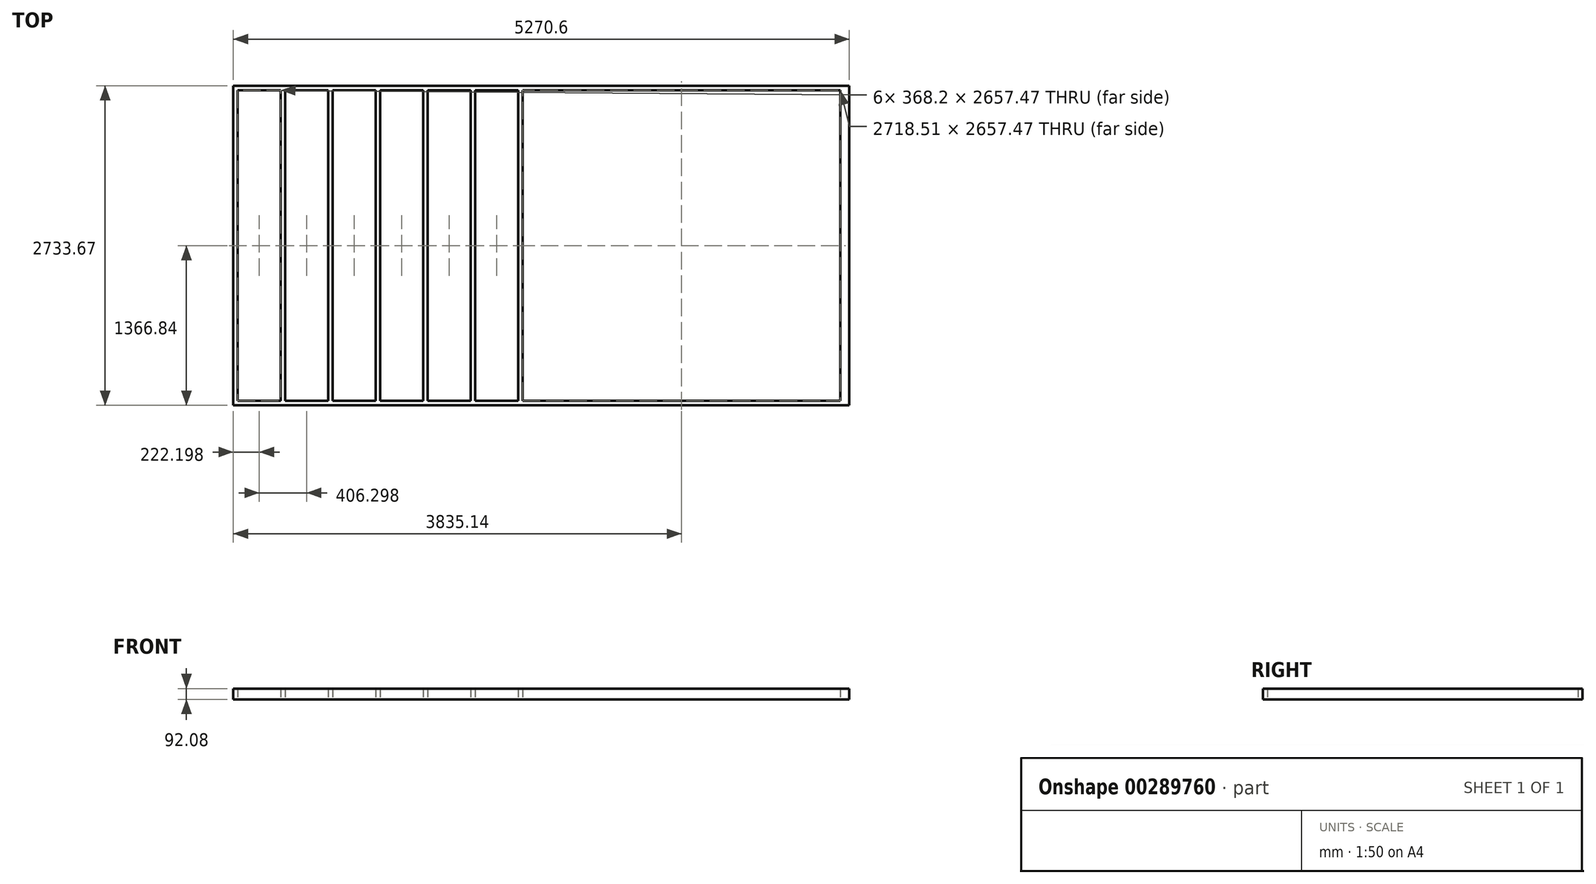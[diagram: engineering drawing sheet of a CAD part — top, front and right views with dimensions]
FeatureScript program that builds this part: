
annotation { "Feature Type Name" : "Feature", "Feature Type Description" : "" }
export const myFeature = defineFeature(function(context is Context, id is Id, definition is map)
    precondition{}
    {
        {
            var Q0;
            Q0=qCreatedBy(makeId("Top.planeOp"),FACE);
            var sketch = newSketch(context, id + "F0", { "sketchPlane" : qUnion([Q0])});
            skLineSegment(sketch, "E0.right", {"start": v(-5575.4, -1219.2) * mm, "end": v(-5575.4, 1514.47) * mm});
            skPoint(sketch, "E0.middle", {"position": v(0, 0) * mm});
            skLineSegment(sketch, "E1", {"start": v(-304.8, 1514.48) * mm, "end": v(-304.8, -1219.2) * mm});
            skLineSegment(sketch, "E2", {"start": v(-5575.4, -1219.2) * mm, "end": v(-304.8, -1219.2) * mm});
            skLineSegment(sketch, "E3.bottom", {"start": v(-5537.3, 1476.37) * mm, "end": v(-342.9, 1476.37) * mm});
            skLineSegment(sketch, "E3.top", {"start": v(-5537.3, -1181.1) * mm, "end": v(-342.9, -1181.1) * mm});
            skLineSegment(sketch, "E3.left", {"start": v(-5537.3, 1476.37) * mm, "end": v(-5537.3, -1181.1) * mm});
            skLineSegment(sketch, "E3.right", {"start": v(-342.9, 1476.38) * mm, "end": v(-342.9, -1181.1) * mm});
            skLineSegment(sketch, "E4.bottom", {"start": v(-5169.1, 1476.37) * mm, "end": v(-5131, 1476.37) * mm});
            skLineSegment(sketch, "E4.top", {"start": v(-5169.1, -1181.1) * mm, "end": v(-5131, -1181.1) * mm});
            skLineSegment(sketch, "E4.left", {"start": v(-5169.1, 1476.37) * mm, "end": v(-5169.1, -1181.1) * mm});
            skLineSegment(sketch, "E4.right", {"start": v(-5131, 1476.37) * mm, "end": v(-5131, -1181.1) * mm});
            skLineSegment(sketch, "E5.bottom", {"start": v(-4762.8, 1476.37) * mm, "end": v(-4724.7, 1476.37) * mm});
            skLineSegment(sketch, "E5.top", {"start": v(-4762.8, -1181.1) * mm, "end": v(-4724.7, -1181.1) * mm});
            skLineSegment(sketch, "E5.left", {"start": v(-4762.8, 1476.37) * mm, "end": v(-4762.8, -1181.1) * mm});
            skLineSegment(sketch, "E5.right", {"start": v(-4724.7, 1476.37) * mm, "end": v(-4724.7, -1181.1) * mm});
            skLineSegment(sketch, "E6.bottom", {"start": v(-4356.5, 1476.37) * mm, "end": v(-4318.4, 1476.37) * mm});
            skLineSegment(sketch, "E6.top", {"start": v(-4356.5, -1181.1) * mm, "end": v(-4318.4, -1181.1) * mm});
            skLineSegment(sketch, "E6.left", {"start": v(-4356.5, 1476.37) * mm, "end": v(-4356.5, -1181.1) * mm});
            skLineSegment(sketch, "E6.right", {"start": v(-4318.4, 1476.37) * mm, "end": v(-4318.4, -1181.1) * mm});
            skLineSegment(sketch, "E7.bottom", {"start": v(-3950.2, 1476.37) * mm, "end": v(-3912.1, 1476.37) * mm});
            skLineSegment(sketch, "E7.top", {"start": v(-3950.2, -1181.1) * mm, "end": v(-3912.1, -1181.1) * mm});
            skLineSegment(sketch, "E7.left", {"start": v(-3950.2, 1476.37) * mm, "end": v(-3950.2, -1181.1) * mm});
            skLineSegment(sketch, "E7.right", {"start": v(-3912.1, 1476.37) * mm, "end": v(-3912.1, -1181.1) * mm});
            skLineSegment(sketch, "E8.bottom", {"start": v(-3543.9, 1476.38) * mm, "end": v(-3505.8, 1476.38) * mm});
            skLineSegment(sketch, "E8.top", {"start": v(-3543.9, -1181.1) * mm, "end": v(-3505.8, -1181.1) * mm});
            skLineSegment(sketch, "E8.left", {"start": v(-3543.9, 1476.37) * mm, "end": v(-3543.9, -1181.1) * mm});
            skLineSegment(sketch, "E8.right", {"start": v(-3505.8, 1476.37) * mm, "end": v(-3505.8, -1181.1) * mm});
            skLineSegment(sketch, "E9.bottom", {"start": v(-3137.61, 1476.38) * mm, "end": v(-3099.51, 1476.38) * mm});
            skLineSegment(sketch, "E9.top", {"start": v(-3137.61, -1181.1) * mm, "end": v(-3099.51, -1181.1) * mm});
            skLineSegment(sketch, "E9.left", {"start": v(-3137.61, 1476.37) * mm, "end": v(-3137.61, -1181.1) * mm});
            skLineSegment(sketch, "E9.right", {"start": v(-3099.51, 1476.37) * mm, "end": v(-3099.51, -1181.1) * mm});
            skLineSegment(sketch, "E10", {"start": v(-3118.56, 1476.37) * mm, "end": v(-3118.56, -1181.1) * mm, "construction": true});
            skLineSegment(sketch, "E11.MirrorCS", {"start": v(-1068.02, 1476.38) * mm, "end": v(-1106.12, 1476.38) * mm});
            skLineSegment(sketch, "E12.MirrorCS", {"start": v(-1068.02, -1181.1) * mm, "end": v(-1106.12, -1181.1) * mm});
            skLineSegment(sketch, "E13.MirrorCS", {"start": v(-2693.21, -1181.1) * mm, "end": v(-2731.31, -1181.1) * mm});
            skLineSegment(sketch, "E14.MirrorCS", {"start": v(-1880.62, -1181.1) * mm, "end": v(-1918.72, -1181.1) * mm});
            skLineSegment(sketch, "E15.MirrorCS", {"start": v(-1880.62, 1476.38) * mm, "end": v(-1918.72, 1476.38) * mm});
            skLineSegment(sketch, "E16.MirrorCS", {"start": v(-1474.32, 1476.38) * mm, "end": v(-1512.42, 1476.38) * mm});
            skLineSegment(sketch, "E17.MirrorCS", {"start": v(-2286.91, 1476.38) * mm, "end": v(-2325.01, 1476.38) * mm});
            skLineSegment(sketch, "E18.MirrorCS", {"start": v(-2693.21, 1476.38) * mm, "end": v(-2731.31, 1476.38) * mm});
            skLineSegment(sketch, "E19.MirrorCS", {"start": v(-1474.32, -1181.1) * mm, "end": v(-1512.42, -1181.1) * mm});
            skLineSegment(sketch, "E20.MirrorCS", {"start": v(-2286.91, -1181.1) * mm, "end": v(-2325.01, -1181.1) * mm});
            skLineSegment(sketch, "E21.MirrorCS", {"start": v(-1474.32, 1476.38) * mm, "end": v(-1474.32, -1181.1) * mm});
            skLineSegment(sketch, "E22.MirrorCS", {"start": v(-2325.01, 1476.37) * mm, "end": v(-2325.01, -1181.1) * mm});
            skLineSegment(sketch, "E23.MirrorCS", {"start": v(-1068.02, 1476.38) * mm, "end": v(-1068.02, -1181.1) * mm});
            skLineSegment(sketch, "E24.MirrorCS", {"start": v(-1512.42, 1476.38) * mm, "end": v(-1512.42, -1181.1) * mm});
            skLineSegment(sketch, "E25.MirrorCS", {"start": v(-1918.72, 1476.37) * mm, "end": v(-1918.72, -1181.1) * mm});
            skLineSegment(sketch, "E26.MirrorCS", {"start": v(-2693.21, 1476.37) * mm, "end": v(-2693.21, -1181.1) * mm});
            skLineSegment(sketch, "E27.MirrorCS", {"start": v(-2286.91, 1476.37) * mm, "end": v(-2286.91, -1181.1) * mm});
            skLineSegment(sketch, "E28.MirrorCS", {"start": v(-1106.12, 1476.37) * mm, "end": v(-1106.12, -1181.1) * mm});
            skLineSegment(sketch, "E29.MirrorCS", {"start": v(-2731.31, 1476.37) * mm, "end": v(-2731.31, -1181.1) * mm});
            skLineSegment(sketch, "E30.MirrorCS", {"start": v(-1880.62, 1476.37) * mm, "end": v(-1880.62, -1181.1) * mm});
            skLineSegment(sketch, "E31", {"start": v(-5575.4, 1514.47) * mm, "end": v(-304.8, 1514.48) * mm});
            skLineSegment(sketch, "E32", {"start": v(-381, 1476.38) * mm, "end": v(-381, -1181.1) * mm});
            skLineSegment(sketch, "E33.bottom", {"start": v(-699.82, 1476.37) * mm, "end": v(-661.72, 1476.37) * mm});
            skLineSegment(sketch, "E33.top", {"start": v(-699.82, -1181.1) * mm, "end": v(-661.72, -1181.1) * mm});
            skLineSegment(sketch, "E33.left", {"start": v(-699.82, 1476.38) * mm, "end": v(-699.82, -1181.1) * mm});
            skLineSegment(sketch, "E33.right", {"start": v(-661.72, 1476.38) * mm, "end": v(-661.72, -1181.1) * mm});
            skSolve(sketch);
        }
        {
            var Q0;
            {var subQ0=sQuery(id+"F0.wireOp",EDGE,"kg6uHfn1-oYHp-dpYk-6MLj-0RLF3WtnhEy7");var subQ1=sQuery(id+"F0.wireOp",EDGE,"8106601b-d97d-4dcf-b6dc-423d0e0e66910.MirrorCS");var subQ2=makeQuery(id+"F0.imprint","INTERSECT",VERTEX,{"derivedFrom":[subQ1,subQ0]});Q0=makeQuery(id+"F0.imprint","IMPRINT",FACE,{"disambiguationData":[TD([[makeQuery(id+"F0.imprint","IMPRINT",EDGE,{"disambiguationData":[TD([[subQ2,-1.0]])],"derivedFrom":subQ1}),1.0]])]});}
            var Q1;
            Q1=makeQuery(id+"F0.imprint","IMPRINT",FACE,{"disambiguationData":[TD([[makeQuery(id+"F0.imprint","IMPRINT",EDGE,{"derivedFrom":sQuery(id+"F0.wireOp",EDGE,"w7in2STq-dmfq-Ztst-uc13-PS53EKAe34f7.bottom")}),-1.0]])]});
            var Q2;
            {var subQ4=sQuery(id+"F0.wireOp",EDGE,"8a681850-bd4a-4ca6-8d45-30870cc5114b0.MirrorCS");var subQ6=sQuery(id+"F0.wireOp",EDGE,"4AthFqkJ-wqFj-7w0H-RTdV-ZVLi3eRejgEJ.bottom");var subQ7=makeQuery(id+"F0.imprint","INTERSECT",VERTEX,{"derivedFrom":[subQ6,subQ4]});Q2=makeQuery(id+"F0.imprint","IMPRINT",FACE,{"disambiguationData":[TD([[makeQuery(id+"F0.imprint","IMPRINT",EDGE,{"disambiguationData":[TD([[subQ7,-1.0]])],"derivedFrom":subQ6}),1.0]])]});}
            var Q3;
            {var subQ5=sQuery(id+"F0.wireOp",EDGE,"eca8af08-4f88-4f9e-b7fb-055b73c8b4f30.MirrorCS");var subQ7=sQuery(id+"F0.wireOp",EDGE,"4AthFqkJ-wqFj-7w0H-RTdV-ZVLi3eRejgEJ.bottom");var subQ8=makeQuery(id+"F0.imprint","INTERSECT",VERTEX,{"derivedFrom":[subQ7,subQ5]});Q3=makeQuery(id+"F0.imprint","IMPRINT",FACE,{"disambiguationData":[TD([[makeQuery(id+"F0.imprint","IMPRINT",EDGE,{"disambiguationData":[TD([[subQ8,-1.0]])],"derivedFrom":subQ7}),1.0]])]});}
            var Q4;
            {var subQ4=sQuery(id+"F0.wireOp",EDGE,"1bcce820-757c-45ce-a4fe-54bff22ba8310.MirrorCS");var subQ6=sQuery(id+"F0.wireOp",EDGE,"4AthFqkJ-wqFj-7w0H-RTdV-ZVLi3eRejgEJ.bottom");var subQ7=makeQuery(id+"F0.imprint","INTERSECT",VERTEX,{"derivedFrom":[subQ6,subQ4]});Q4=makeQuery(id+"F0.imprint","IMPRINT",FACE,{"disambiguationData":[TD([[makeQuery(id+"F0.imprint","IMPRINT",EDGE,{"disambiguationData":[TD([[subQ7,-1.0]])],"derivedFrom":subQ6}),1.0]])]});}
            var Q5;
            {var subQ4=sQuery(id+"F0.wireOp",EDGE,"4AthFqkJ-wqFj-7w0H-RTdV-ZVLi3eRejgEJ.left");Q5=makeQuery(id+"F0.imprint","IMPRINT",FACE,{"disambiguationData":[TD([[makeQuery(id+"F0.imprint","IMPRINT",EDGE,{"derivedFrom":subQ4}),-1.0]])]});}
            var Q6;
            {var subQ4=sQuery(id+"F0.wireOp",EDGE,"1XwIb5Eg-bF9u-TIWm-DKcX-weKEORKnCqGm.bottom");var subQ7=sQuery(id+"F0.wireOp",EDGE,"1bcce820-757c-45ce-a4fe-54bff22ba8310.MirrorCS");var subQ10=makeQuery(id+"F0.imprint","INTERSECT",VERTEX,{"derivedFrom":[subQ4,subQ7]});Q6=makeQuery(id+"F0.imprint","IMPRINT",FACE,{"disambiguationData":[TD([[makeQuery(id+"F0.imprint","IMPRINT",EDGE,{"disambiguationData":[TD([[subQ10,-1.0]])],"derivedFrom":subQ4}),-1.0]])]});}
            var Q7;
            {var subQ6=sQuery(id+"F0.wireOp",EDGE,"1XwIb5Eg-bF9u-TIWm-DKcX-weKEORKnCqGm.left");Q7=makeQuery(id+"F0.imprint","IMPRINT",FACE,{"disambiguationData":[TD([[makeQuery(id+"F0.imprint","IMPRINT",EDGE,{"derivedFrom":subQ6}),1.0]])]});}
            var Q8;
            {var subQ4=sQuery(id+"F0.wireOp",EDGE,"1XwIb5Eg-bF9u-TIWm-DKcX-weKEORKnCqGm.bottom");var subQ7=sQuery(id+"F0.wireOp",EDGE,"eca8af08-4f88-4f9e-b7fb-055b73c8b4f30.MirrorCS");var subQ9=makeQuery(id+"F0.imprint","INTERSECT",VERTEX,{"derivedFrom":[subQ4,subQ7]});Q8=makeQuery(id+"F0.imprint","IMPRINT",FACE,{"disambiguationData":[TD([[makeQuery(id+"F0.imprint","IMPRINT",EDGE,{"disambiguationData":[TD([[subQ9,-1.0]])],"derivedFrom":subQ4}),-1.0]])]});}
            var Q9;
            {var subQ3=sQuery(id+"F0.wireOp",EDGE,"8a681850-bd4a-4ca6-8d45-30870cc5114b0.MirrorCS");var subQ6=sQuery(id+"F0.wireOp",EDGE,"1XwIb5Eg-bF9u-TIWm-DKcX-weKEORKnCqGm.bottom");var subQ7=makeQuery(id+"F0.imprint","INTERSECT",VERTEX,{"derivedFrom":[subQ6,subQ3]});Q9=makeQuery(id+"F0.imprint","IMPRINT",FACE,{"disambiguationData":[TD([[makeQuery(id+"F0.imprint","IMPRINT",EDGE,{"disambiguationData":[TD([[subQ7,-1.0]])],"derivedFrom":subQ6}),-1.0]])]});}
            var Q10;
            {var subQ0=sQuery(id+"F0.wireOp",EDGE,"573c87d8-b675-496e-a079-9395e3357b8d0.MirrorCS");Q10=makeQuery(id+"F0.imprint","IMPRINT",FACE,{"disambiguationData":[TD([[makeQuery(id+"F0.imprint","IMPRINT",EDGE,{"derivedFrom":subQ0}),1.0]])]});}
            var Q11;
            {var subQ0=sQuery(id+"F0.wireOp",EDGE,"edbdd21b-7951-4497-ac7e-6e46abb4ccd70.MirrorCS");Q11=makeQuery(id+"F0.imprint","IMPRINT",FACE,{"disambiguationData":[TD([[makeQuery(id+"F0.imprint","IMPRINT",EDGE,{"derivedFrom":subQ0}),-1.0]])]});}
            var Q12;
            Q12=makeQuery(id+"F0.imprint","IMPRINT",FACE,{"disambiguationData":[TD([[makeQuery(id+"F0.imprint","IMPRINT",EDGE,{"derivedFrom":sQuery(id+"F0.wireOp",EDGE,"xTM1oSQN-q9p7-LrQJ-wgkP-syFjsQtJfwuK.bottom")}),-1.0]])]});
            var Q13;
            {var subQ0=sQuery(id+"F0.wireOp",EDGE,"7de17b8e-8469-475a-b975-fd82b060c23f0.MirrorCS");Q13=makeQuery(id+"F0.imprint","IMPRINT",FACE,{"disambiguationData":[TD([[makeQuery(id+"F0.imprint","IMPRINT",EDGE,{"derivedFrom":subQ0}),1.0]])]});}
            var Q14;
            {var subQ0=sQuery(id+"F0.wireOp",EDGE,"e03bbd14-4e46-43d8-a5f9-80b2dea7db7f0.MirrorCS");Q14=makeQuery(id+"F0.imprint","IMPRINT",FACE,{"disambiguationData":[TD([[makeQuery(id+"F0.imprint","IMPRINT",EDGE,{"derivedFrom":subQ0}),1.0]])]});}
            var Q15;
            {var subQ0=sQuery(id+"F0.wireOp",EDGE,"1b0e9755-274d-47f2-9ad2-c5868fe4f0aa0.MirrorCS");Q15=makeQuery(id+"F0.imprint","IMPRINT",FACE,{"disambiguationData":[TD([[makeQuery(id+"F0.imprint","IMPRINT",EDGE,{"derivedFrom":subQ0}),1.0]])]});}
            var Q16;
            {var subQ0=sQuery(id+"F0.wireOp",EDGE,"0493b29f-ec4a-4c4c-ac9e-8fdb3be76d310.MirrorCS");Q16=makeQuery(id+"F0.imprint","IMPRINT",FACE,{"disambiguationData":[TD([[makeQuery(id+"F0.imprint","IMPRINT",EDGE,{"derivedFrom":subQ0}),1.0]])]});}
            var Q17;
            {var subQ0=sQuery(id+"F0.wireOp",EDGE,"9fe0fe99-07bc-4679-9664-f55d6f2dc43d0.MirrorCS");Q17=makeQuery(id+"F0.imprint","IMPRINT",FACE,{"disambiguationData":[TD([[makeQuery(id+"F0.imprint","IMPRINT",EDGE,{"derivedFrom":subQ0}),1.0]])]});}
            var Q18;
            {var subQ7=sQuery(id+"F0.wireOp",EDGE,"1XwIb5Eg-bF9u-TIWm-DKcX-weKEORKnCqGm.right");Q18=makeQuery(id+"F0.imprint","IMPRINT",FACE,{"disambiguationData":[TD([[makeQuery(id+"F0.imprint","IMPRINT",EDGE,{"derivedFrom":subQ7}),-1.0]])]});}
            var Q19;
            {var subQ3=sQuery(id+"F0.wireOp",EDGE,"cGS8tV0A-mpKU-2uX5-CStv-OkKF9vKUYxA9");Q19=makeQuery(id+"F0.imprint","IMPRINT",FACE,{"disambiguationData":[TD([[makeQuery(id+"F0.imprint","IMPRINT",EDGE,{"derivedFrom":subQ3}),1.0]])]});}
            var Q20;
            {var subQ0=sQuery(id+"F0.wireOp",EDGE,"3EoNbSYs-SzWb-u8DF-ybgV-jMauNVkNRy9z.bottom");Q20=makeQuery(id+"F0.imprint","IMPRINT",FACE,{"disambiguationData":[TD([[makeQuery(id+"F0.imprint","IMPRINT",EDGE,{"derivedFrom":subQ0}),1.0]])]});}
            var Q21;
            {var subQ3=sQuery(id+"F0.wireOp",EDGE,"4AthFqkJ-wqFj-7w0H-RTdV-ZVLi3eRejgEJ.right");Q21=makeQuery(id+"F0.imprint","IMPRINT",FACE,{"disambiguationData":[TD([[makeQuery(id+"F0.imprint","IMPRINT",EDGE,{"derivedFrom":subQ3}),1.0]])]});}
            var Q22;
            {var subQ5=sQuery(id+"F0.wireOp",EDGE,"0632b321-56e7-4b31-9cd1-585e07a893ff0.MirrorCS");var subQ6=sQuery(id+"F0.wireOp",EDGE,"1XwIb5Eg-bF9u-TIWm-DKcX-weKEORKnCqGm.bottom");var subQ7=makeQuery(id+"F0.imprint","INTERSECT",VERTEX,{"derivedFrom":[subQ6,subQ5]});Q22=makeQuery(id+"F0.imprint","IMPRINT",FACE,{"disambiguationData":[TD([[makeQuery(id+"F0.imprint","IMPRINT",EDGE,{"disambiguationData":[TD([[subQ7,-1.0]])],"derivedFrom":subQ6}),-1.0]])]});}
            var Q23;
            {var subQ4=sQuery(id+"F0.wireOp",EDGE,"e9220ee2-881e-495c-a7c1-f9c4819509570.MirrorCS");Q23=makeQuery(id+"F0.imprint","IMPRINT",FACE,{"disambiguationData":[TD([[makeQuery(id+"F0.imprint","IMPRINT",EDGE,{"derivedFrom":subQ4}),-1.0]])]});}
            var Q24;
            {var subQ4=sQuery(id+"F0.wireOp",EDGE,"e9220ee2-881e-495c-a7c1-f9c4819509570.MirrorCS");Q24=makeQuery(id+"F0.imprint","IMPRINT",FACE,{"disambiguationData":[TD([[makeQuery(id+"F0.imprint","IMPRINT",EDGE,{"derivedFrom":subQ4}),-1.0]])]});}
            var Q25;
            {var subQ0=sQuery(id+"F0.wireOp",EDGE,"3EoNbSYs-SzWb-u8DF-ybgV-jMauNVkNRy9z.top");Q25=makeQuery(id+"F0.imprint","IMPRINT",FACE,{"disambiguationData":[TD([[makeQuery(id+"F0.imprint","IMPRINT",EDGE,{"derivedFrom":subQ0}),-1.0]])]});}
            var Q26;
            {var subQ0=sQuery(id+"F0.wireOp",EDGE,"aInlmaS3-BiLq-Bbma-6VfX-RYyb0QgMCohg");Q26=makeQuery(id+"F0.imprint","IMPRINT",FACE,{"disambiguationData":[TD([[makeQuery(id+"F0.imprint","IMPRINT",EDGE,{"derivedFrom":subQ0}),1.0]])]});}
            var Q27;
            {var subQ1=sQuery(id+"F0.wireOp",EDGE,"6dIbjfUG-IAKx-LzC9-qQtg-bTm0nvSxZE7U");Q27=makeQuery(id+"F0.imprint","IMPRINT",FACE,{"disambiguationData":[TD([[makeQuery(id+"F0.imprint","IMPRINT",EDGE,{"derivedFrom":subQ1}),-1.0]])]});}
            var Q28;
            {var subQ3=sQuery(id+"F0.wireOp",EDGE,"6dIbjfUG-IAKx-LzC9-qQtg-bTm0nvSxZE7U");Q28=makeQuery(id+"F0.imprint","IMPRINT",FACE,{"disambiguationData":[TD([[makeQuery(id+"F0.imprint","IMPRINT",EDGE,{"derivedFrom":subQ3}),1.0]])]});}
            var Q29;
            {var subQ2=sQuery(id+"F0.wireOp",EDGE,"PrKW4Dy4-RNk2-6Oy2-wL3X-jKJNfqZvHOta");var subQ4=sQuery(id+"F0.wireOp",EDGE,"1XwIb5Eg-bF9u-TIWm-DKcX-weKEORKnCqGm.top");var subQ5=makeQuery(id+"F0.imprint","INTERSECT",VERTEX,{"derivedFrom":[subQ4,subQ2]});Q29=makeQuery(id+"F0.imprint","IMPRINT",FACE,{"disambiguationData":[TD([[makeQuery(id+"F0.imprint","IMPRINT",EDGE,{"disambiguationData":[TD([[subQ5,1.0]])],"derivedFrom":subQ2}),-1.0]])]});}
            var Q30;
            {var subQ0=sQuery(id+"F0.wireOp",EDGE,"AWdK3n0U-rIrt-pWfR-QOIf-b13k28BsWoug");Q30=makeQuery(id+"F0.imprint","IMPRINT",FACE,{"disambiguationData":[TD([[makeQuery(id+"F0.imprint","IMPRINT",EDGE,{"derivedFrom":subQ0}),1.0]])]});}
            var Q31;
            {var subQ0=sQuery(id+"F0.wireOp",EDGE,"kg6uHfn1-oYHp-dpYk-6MLj-0RLF3WtnhEy7");var subQ1=sQuery(id+"F0.wireOp",EDGE,"f709e9b3-6885-4daf-8f0c-d59ee65569a90.MirrorCS");var subQ2=makeQuery(id+"F0.imprint","INTERSECT",VERTEX,{"derivedFrom":[subQ1,subQ0]});Q31=makeQuery(id+"F0.imprint","IMPRINT",FACE,{"disambiguationData":[TD([[makeQuery(id+"F0.imprint","IMPRINT",EDGE,{"disambiguationData":[TD([[subQ2,-1.0]])],"derivedFrom":subQ1}),1.0]])]});}
            var Q32;
            {var subQ0=sQuery(id+"F0.wireOp",EDGE,"kg6uHfn1-oYHp-dpYk-6MLj-0RLF3WtnhEy7");var subQ2=sQuery(id+"F0.wireOp",EDGE,"5f963c61-5f66-4834-8852-3989dfd0aaaa0.MirrorCS");var subQ3=makeQuery(id+"F0.imprint","INTERSECT",VERTEX,{"derivedFrom":[subQ2,subQ0]});Q32=makeQuery(id+"F0.imprint","IMPRINT",FACE,{"disambiguationData":[TD([[makeQuery(id+"F0.imprint","IMPRINT",EDGE,{"disambiguationData":[TD([[subQ3,-1.0]])],"derivedFrom":subQ2}),1.0]])]});}
            var Q33;
            {var subQ0=sQuery(id+"F0.wireOp",EDGE,"xECrVSvC-3TnS-PIpk-5k4f-ELXDZuZoR2Xq");Q33=makeQuery(id+"F0.imprint","IMPRINT",FACE,{"disambiguationData":[TD([[makeQuery(id+"F0.imprint","IMPRINT",EDGE,{"derivedFrom":subQ0}),-1.0]])]});}
            var Q34;
            {var subQ0=sQuery(id+"F0.wireOp",EDGE,"DsOPnhS2-WDv3-fEhJ-uP2v-zB4hWMM1ggMi");Q34=makeQuery(id+"F0.imprint","IMPRINT",FACE,{"disambiguationData":[TD([[makeQuery(id+"F0.imprint","IMPRINT",EDGE,{"derivedFrom":subQ0}),-1.0]])]});}
            var Q35;
            {var subQ6=sQuery(id+"F0.wireOp",EDGE,"OtMJ0CzN-JfN0-Mc7h-kQnT-5fw6SVZFctJd");Q35=makeQuery(id+"F0.imprint","IMPRINT",FACE,{"disambiguationData":[TD([[makeQuery(id+"F0.imprint","IMPRINT",EDGE,{"derivedFrom":subQ6}),1.0]])]});}
            var Q36;
            {var subQ0=sQuery(id+"F0.wireOp",EDGE,"BXZ3mWxO-t787-7BjH-HfK1-pwCE8oRwYUB0");Q36=makeQuery(id+"F0.imprint","IMPRINT",FACE,{"disambiguationData":[TD([[makeQuery(id+"F0.imprint","IMPRINT",EDGE,{"derivedFrom":subQ0}),-1.0]])]});}
            var Q37;
            {var subQ4=sQuery(id+"F0.wireOp",EDGE,"rltV0tBx-ZmDJ-Ag2v-8vYA-OFwq6olGCcpk");Q37=makeQuery(id+"F0.imprint","IMPRINT",FACE,{"disambiguationData":[TD([[makeQuery(id+"F0.imprint","IMPRINT",EDGE,{"derivedFrom":subQ4}),1.0]])]});}
            var Q38;
            Q38=makeQuery(id+"F0.imprint","IMPRINT",FACE,{"disambiguationData":[TD([[makeQuery(id+"F0.imprint","IMPRINT",EDGE,{"derivedFrom":sQuery(id+"F0.wireOp",EDGE,"E0.right")}),-1.0]])]});
            var Q39;
            {var subQ0=sQuery(id+"F0.wireOp",EDGE,"E4.left");Q39=makeQuery(id+"F0.imprint","IMPRINT",FACE,{"disambiguationData":[TD([[makeQuery(id+"F0.imprint","IMPRINT",EDGE,{"derivedFrom":subQ0}),1.0]])]});}
            var Q40;
            {var subQ0=sQuery(id+"F0.wireOp",EDGE,"E5.left");Q40=makeQuery(id+"F0.imprint","IMPRINT",FACE,{"disambiguationData":[TD([[makeQuery(id+"F0.imprint","IMPRINT",EDGE,{"derivedFrom":subQ0}),1.0]])]});}
            var Q41;
            {var subQ0=sQuery(id+"F0.wireOp",EDGE,"E6.left");Q41=makeQuery(id+"F0.imprint","IMPRINT",FACE,{"disambiguationData":[TD([[makeQuery(id+"F0.imprint","IMPRINT",EDGE,{"derivedFrom":subQ0}),1.0]])]});}
            var Q42;
            {var subQ0=sQuery(id+"F0.wireOp",EDGE,"E7.left");Q42=makeQuery(id+"F0.imprint","IMPRINT",FACE,{"disambiguationData":[TD([[makeQuery(id+"F0.imprint","IMPRINT",EDGE,{"derivedFrom":subQ0}),1.0]])]});}
            var Q43;
            {var subQ0=sQuery(id+"F0.wireOp",EDGE,"E8.left");Q43=makeQuery(id+"F0.imprint","IMPRINT",FACE,{"disambiguationData":[TD([[makeQuery(id+"F0.imprint","IMPRINT",EDGE,{"derivedFrom":subQ0}),1.0]])]});}
            var Q44;
            {var subQ0=sQuery(id+"F0.wireOp",EDGE,"E9.left");Q44=makeQuery(id+"F0.imprint","IMPRINT",FACE,{"disambiguationData":[TD([[makeQuery(id+"F0.imprint","IMPRINT",EDGE,{"derivedFrom":subQ0}),1.0]])]});}
            var Q45;
            {var subQ0=sQuery(id+"F0.wireOp",EDGE,"d8ddfb4b-c561-4c4d-a629-e70af5e53a8a13.MirrorCS");Q45=makeQuery(id+"F0.imprint","IMPRINT",FACE,{"disambiguationData":[TD([[makeQuery(id+"F0.imprint","IMPRINT",EDGE,{"derivedFrom":subQ0}),-1.0]])]});}
            var Q46;
            {var subQ0=sQuery(id+"F0.wireOp",EDGE,"d8ddfb4b-c561-4c4d-a629-e70af5e53a8a11.MirrorCS");Q46=makeQuery(id+"F0.imprint","IMPRINT",FACE,{"disambiguationData":[TD([[makeQuery(id+"F0.imprint","IMPRINT",EDGE,{"derivedFrom":subQ0}),-1.0]])]});}
            var Q47;
            {var subQ0=sQuery(id+"F0.wireOp",EDGE,"d8ddfb4b-c561-4c4d-a629-e70af5e53a8a16.MirrorCS");Q47=makeQuery(id+"F0.imprint","IMPRINT",FACE,{"disambiguationData":[TD([[makeQuery(id+"F0.imprint","IMPRINT",EDGE,{"derivedFrom":subQ0}),-1.0]])]});}
            var Q48;
            {var subQ0=sQuery(id+"F0.wireOp",EDGE,"d8ddfb4b-c561-4c4d-a629-e70af5e53a8a10.MirrorCS");Q48=makeQuery(id+"F0.imprint","IMPRINT",FACE,{"disambiguationData":[TD([[makeQuery(id+"F0.imprint","IMPRINT",EDGE,{"derivedFrom":subQ0}),1.0]])]});}
            var Q49;
            {var subQ0=sQuery(id+"F0.wireOp",EDGE,"d8ddfb4b-c561-4c4d-a629-e70af5e53a8a14.MirrorCS");Q49=makeQuery(id+"F0.imprint","IMPRINT",FACE,{"disambiguationData":[TD([[makeQuery(id+"F0.imprint","IMPRINT",EDGE,{"derivedFrom":subQ0}),-1.0]])]});}
            var Q50;
            Q50=makeQuery(id+"F0.imprint","IMPRINT",FACE,{"disambiguationData":[TD([[makeQuery(id+"F0.imprint","IMPRINT",EDGE,{"derivedFrom":sQuery(id+"F0.wireOp",EDGE,"144fd146-0914-4e58-99f4-28c89aa4e7bd7.MirrorCS")}),1.0]])]});
            var Q51;
            Q51=makeQuery(id+"F0.imprint","IMPRINT",FACE,{"disambiguationData":[TD([[makeQuery(id+"F0.imprint","IMPRINT",EDGE,{"derivedFrom":sQuery(id+"F0.wireOp",EDGE,"144fd146-0914-4e58-99f4-28c89aa4e7bd0.MirrorCS")}),-1.0]])]});
            var Q52;
            Q52=makeQuery(id+"F0.imprint","IMPRINT",FACE,{"disambiguationData":[TD([[makeQuery(id+"F0.imprint","IMPRINT",EDGE,{"derivedFrom":sQuery(id+"F0.wireOp",EDGE,"144fd146-0914-4e58-99f4-28c89aa4e7bd6.MirrorCS")}),1.0]])]});
            var Q53;
            Q53=makeQuery(id+"F0.imprint","IMPRINT",FACE,{"disambiguationData":[TD([[makeQuery(id+"F0.imprint","IMPRINT",EDGE,{"derivedFrom":sQuery(id+"F0.wireOp",EDGE,"144fd146-0914-4e58-99f4-28c89aa4e7bd3.MirrorCS")}),1.0]])]});
            var Q54;
            Q54=makeQuery(id+"F0.imprint","IMPRINT",FACE,{"disambiguationData":[TD([[makeQuery(id+"F0.imprint","IMPRINT",EDGE,{"derivedFrom":sQuery(id+"F0.wireOp",EDGE,"144fd146-0914-4e58-99f4-28c89aa4e7bd1.MirrorCS")}),1.0]])]});
            var Q55;
            Q55=makeQuery(id+"F0.imprint","IMPRINT",FACE,{"disambiguationData":[TD([[makeQuery(id+"F0.imprint","IMPRINT",EDGE,{"derivedFrom":sQuery(id+"F0.wireOp",EDGE,"E13.MirrorCS")}),-1.0]])]});
            var Q56;
            Q56=makeQuery(id+"F0.imprint","IMPRINT",FACE,{"disambiguationData":[TD([[makeQuery(id+"F0.imprint","IMPRINT",EDGE,{"derivedFrom":sQuery(id+"F0.wireOp",EDGE,"E17.MirrorCS")}),1.0]])]});
            var Q57;
            Q57=makeQuery(id+"F0.imprint","IMPRINT",FACE,{"disambiguationData":[TD([[makeQuery(id+"F0.imprint","IMPRINT",EDGE,{"derivedFrom":sQuery(id+"F0.wireOp",EDGE,"E14.MirrorCS")}),-1.0]])]});
            var Q58;
            Q58=makeQuery(id+"F0.imprint","IMPRINT",FACE,{"disambiguationData":[TD([[makeQuery(id+"F0.imprint","IMPRINT",EDGE,{"derivedFrom":sQuery(id+"F0.wireOp",EDGE,"E16.MirrorCS")}),1.0]])]});
            var Q59;
            Q59=makeQuery(id+"F0.imprint","IMPRINT",FACE,{"disambiguationData":[TD([[makeQuery(id+"F0.imprint","IMPRINT",EDGE,{"derivedFrom":sQuery(id+"F0.wireOp",EDGE,"E11.MirrorCS")}),1.0]])]});
            var Q60;
            {var subQ0=sQuery(id+"F0.wireOp",EDGE,"E3.right");Q60=makeQuery(id+"F0.imprint","IMPRINT",FACE,{"disambiguationData":[TD([[makeQuery(id+"F0.imprint","IMPRINT",EDGE,{"derivedFrom":subQ0}),-1.0]])]});}
            var Q61;
            Q61=makeQuery(id+"F0.imprint","IMPRINT",FACE,{"disambiguationData":[TD([[makeQuery(id+"F0.imprint","IMPRINT",EDGE,{"derivedFrom":sQuery(id+"F0.wireOp",EDGE,"E33.bottom")}),-1.0]])]});
            extrude(context, id + "F1", {"entities" : qUnion([Q0, Q1, Q2, Q3, Q4, Q5, Q6, Q7, Q8, Q9, Q10, Q11, Q12, Q13, Q14, Q15, Q16, Q17, Q18, Q19, Q20, Q21, Q22, Q23, Q24, Q25, Q26, Q27, Q28, Q29, Q30, Q31, Q32, Q33, Q34, Q35, Q36, Q37, Q38, Q39, Q40, Q41, Q42, Q43, Q44, Q45, Q46, Q47, Q48, Q49, Q50, Q51, Q52, Q53, Q54, Q55, Q56, Q57, Q58, Q59, Q60, Q61]), "offsetDistance" : 30.48 * mm, "depth" : 92.08 * mm});
        }
    });
